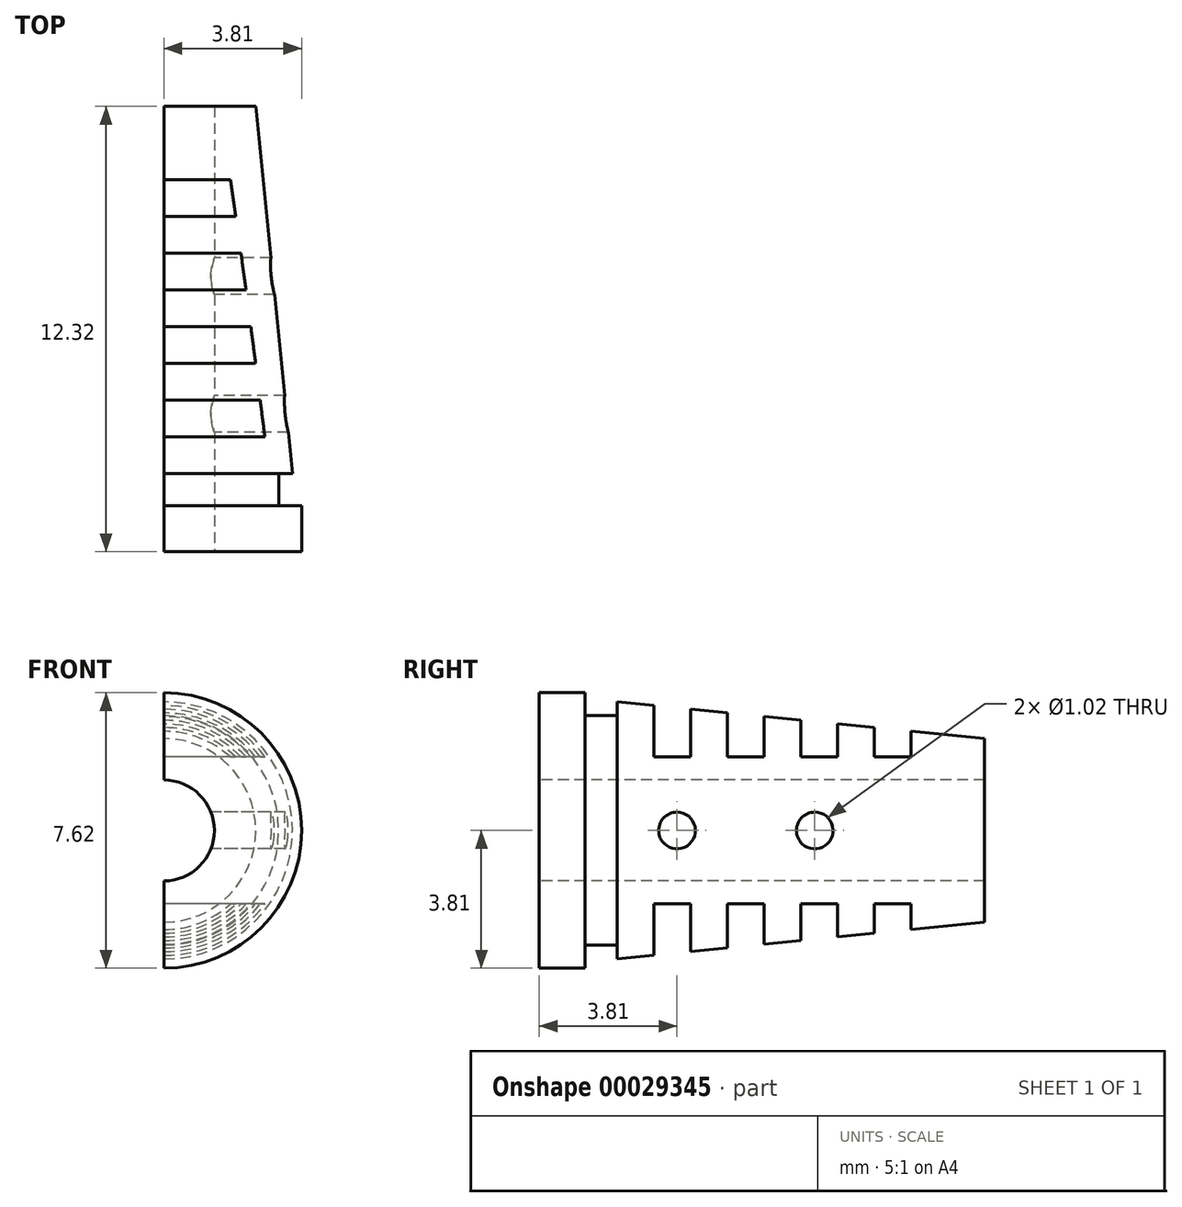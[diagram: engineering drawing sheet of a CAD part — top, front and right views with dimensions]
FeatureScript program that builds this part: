
annotation { "Feature Type Name" : "Feature", "Feature Type Description" : "" }
export const myFeature = defineFeature(function(context is Context, id is Id, definition is map)
    precondition{}
    {
        {
            var Q0;
            Q0=qCreatedBy(makeId("Right.planeOp"),FACE);
            var sketch = newSketch(context, id + "F0", { "sketchPlane" : qUnion([Q0])});
            skLineSegment(sketch, "E0.bottom", {"start": v(0, 0) * mm, "end": v(1.27, 0) * mm});
            skLineSegment(sketch, "E0.top", {"start": v(0, 3.81) * mm, "end": v(1.27, 3.81) * mm});
            skLineSegment(sketch, "E0.left", {"start": v(0, 0) * mm, "end": v(0, 3.81) * mm});
            skLineSegment(sketch, "E0.right", {"start": v(1.27, 0) * mm, "end": v(1.27, 3.81) * mm});
            skLineSegment(sketch, "E1.bottom", {"start": v(1.27, 0) * mm, "end": v(2.16, 0) * mm});
            skLineSegment(sketch, "E1.top", {"start": v(1.27, 3.18) * mm, "end": v(2.16, 3.18) * mm});
            skLineSegment(sketch, "E1.left", {"start": v(1.27, 0) * mm, "end": v(1.27, 3.17) * mm});
            skLineSegment(sketch, "E1.right", {"start": v(2.16, 0) * mm, "end": v(2.16, 3.18) * mm});
            skLineSegment(sketch, "E2", {"start": v(2.16, 0) * mm, "end": v(2.16, 3.56) * mm});
            skLineSegment(sketch, "E3", {"start": v(12.32, 0) * mm, "end": v(2.16, 0) * mm});
            skLineSegment(sketch, "E4", {"start": v(12.32, 0) * mm, "end": v(12.32, 2.54) * mm});
            skLineSegment(sketch, "E5", {"start": v(2.16, 3.56) * mm, "end": v(12.32, 2.54) * mm});
            skSolve(sketch);
        }
        {
            var Q0;
            Q0 = qSketchRegion(id + "F0", true);
            var Q1;
            Q1=sQuery(id+"F0.wireOp",EDGE,"E3");
            revolve(context, id + "F1", {"entities" : qUnion([Q0]), "axis" : qUnion([Q1]), "revolveType" : RevolveType.ONE_DIRECTION, "oppositeDirection" : true, "angle" : 180 * degree});
        }
        {
            var Q0;
            Q0=qCreatedBy(makeId("Front.planeOp"),FACE);
            var sketch = newSketch(context, id + "F2", { "sketchPlane" : qUnion([Q0])});
            skCircle(sketch, "E6", {"center": v(0, 0) * mm, "radius": 1.4 * mm});
            skSolve(sketch);
        }
        {
            var Q0;
            Q0=makeQuery(id+"F2.imprint","IMPRINT",FACE,{"disambiguationData":[TD([[makeQuery(id+"F2.imprint","IMPRINT",EDGE,{"derivedFrom":sQuery(id+"F2.wireOp",EDGE,"E6")}),1.0]])]});
            extrude(context, id + "F3", {"entities" : qUnion([Q0]), "operationType" : NewBodyOperationType.REMOVE, "oppositeDirection" : true, "depth" : 25.4 * mm});
        }
        {
            var Q0;
            Q0=qCreatedBy(makeId("Right.planeOp"),FACE);
            var sketch = newSketch(context, id + "F4", { "sketchPlane" : qUnion([Q0])});
            skLineSegment(sketch, "E7.bottom", {"start": v(3.17, 3.56) * mm, "end": v(4.2, 3.56) * mm});
            skLineSegment(sketch, "E7.top", {"start": v(3.17, 2.03) * mm, "end": v(4.2, 2.03) * mm});
            skLineSegment(sketch, "E7.left", {"start": v(3.17, 3.56) * mm, "end": v(3.17, 2.03) * mm});
            skLineSegment(sketch, "E7.right", {"start": v(4.2, 3.56) * mm, "end": v(4.2, 2.03) * mm});
            skLineSegment(sketch, "E8.bottom", {"start": v(5.2, 3.56) * mm, "end": v(6.22, 3.56) * mm});
            skLineSegment(sketch, "E8.top", {"start": v(5.2, 2.03) * mm, "end": v(6.22, 2.03) * mm});
            skLineSegment(sketch, "E8.left", {"start": v(5.2, 3.56) * mm, "end": v(5.2, 2.03) * mm});
            skLineSegment(sketch, "E8.right", {"start": v(6.22, 3.56) * mm, "end": v(6.22, 2.03) * mm});
            skLineSegment(sketch, "E9.bottom", {"start": v(7.24, 3.56) * mm, "end": v(8.26, 3.56) * mm});
            skLineSegment(sketch, "E9.top", {"start": v(7.24, 2.03) * mm, "end": v(8.26, 2.03) * mm});
            skLineSegment(sketch, "E9.left", {"start": v(7.24, 3.56) * mm, "end": v(7.24, 2.03) * mm});
            skLineSegment(sketch, "E9.right", {"start": v(8.26, 3.56) * mm, "end": v(8.26, 2.03) * mm});
            skLineSegment(sketch, "E10.bottom", {"start": v(9.27, 3.56) * mm, "end": v(10.29, 3.56) * mm});
            skLineSegment(sketch, "E10.top", {"start": v(9.27, 2.03) * mm, "end": v(10.29, 2.03) * mm});
            skLineSegment(sketch, "E10.left", {"start": v(9.27, 3.56) * mm, "end": v(9.27, 2.03) * mm});
            skLineSegment(sketch, "E10.right", {"start": v(10.29, 3.56) * mm, "end": v(10.29, 2.03) * mm});
            skCircle(sketch, "E11", {"center": v(3.81, 0) * mm, "radius": 0.5 * mm});
            skCircle(sketch, "E12", {"center": v(7.62, 0) * mm, "radius": 0.5 * mm});
            skLineSegment(sketch, "E13.bottom", {"start": v(3.18, -2.03) * mm, "end": v(4.2, -2.03) * mm});
            skLineSegment(sketch, "E13.top", {"start": v(3.17, -3.56) * mm, "end": v(4.2, -3.56) * mm});
            skLineSegment(sketch, "E13.left", {"start": v(3.17, -2.03) * mm, "end": v(3.17, -3.56) * mm});
            skLineSegment(sketch, "E13.right", {"start": v(4.2, -2.03) * mm, "end": v(4.2, -3.56) * mm});
            skLineSegment(sketch, "E14.bottom", {"start": v(5.2, -2.03) * mm, "end": v(6.22, -2.03) * mm});
            skLineSegment(sketch, "E14.top", {"start": v(5.2, -3.56) * mm, "end": v(6.22, -3.56) * mm});
            skLineSegment(sketch, "E14.left", {"start": v(5.2, -2.03) * mm, "end": v(5.2, -3.56) * mm});
            skLineSegment(sketch, "E14.right", {"start": v(6.22, -2.03) * mm, "end": v(6.22, -3.56) * mm});
            skLineSegment(sketch, "E15.bottom", {"start": v(7.24, -2.03) * mm, "end": v(8.25, -2.03) * mm});
            skLineSegment(sketch, "E15.top", {"start": v(7.24, -3.56) * mm, "end": v(8.25, -3.56) * mm});
            skLineSegment(sketch, "E15.left", {"start": v(7.24, -2.03) * mm, "end": v(7.24, -3.56) * mm});
            skLineSegment(sketch, "E15.right", {"start": v(8.25, -2.03) * mm, "end": v(8.25, -3.56) * mm});
            skLineSegment(sketch, "E16.bottom", {"start": v(9.27, -2.03) * mm, "end": v(10.29, -2.03) * mm});
            skLineSegment(sketch, "E16.top", {"start": v(9.27, -3.56) * mm, "end": v(10.29, -3.56) * mm});
            skLineSegment(sketch, "E16.left", {"start": v(9.27, -2.03) * mm, "end": v(9.27, -3.56) * mm});
            skLineSegment(sketch, "E16.right", {"start": v(10.29, -2.03) * mm, "end": v(10.29, -3.56) * mm});
            skLineSegment(sketch, "E17", {"start": v(10.29, -2.03) * mm, "end": v(3.17, -2.03) * mm, "construction": true});
            skSolve(sketch);
        }
        {
            var Q0;
            Q0 = qSketchRegion(id + "F4", true);
            extrude(context, id + "F5", {"entities" : qUnion([Q0]), "operationType" : NewBodyOperationType.REMOVE, "depth" : 25.4 * mm});
        }
    });
